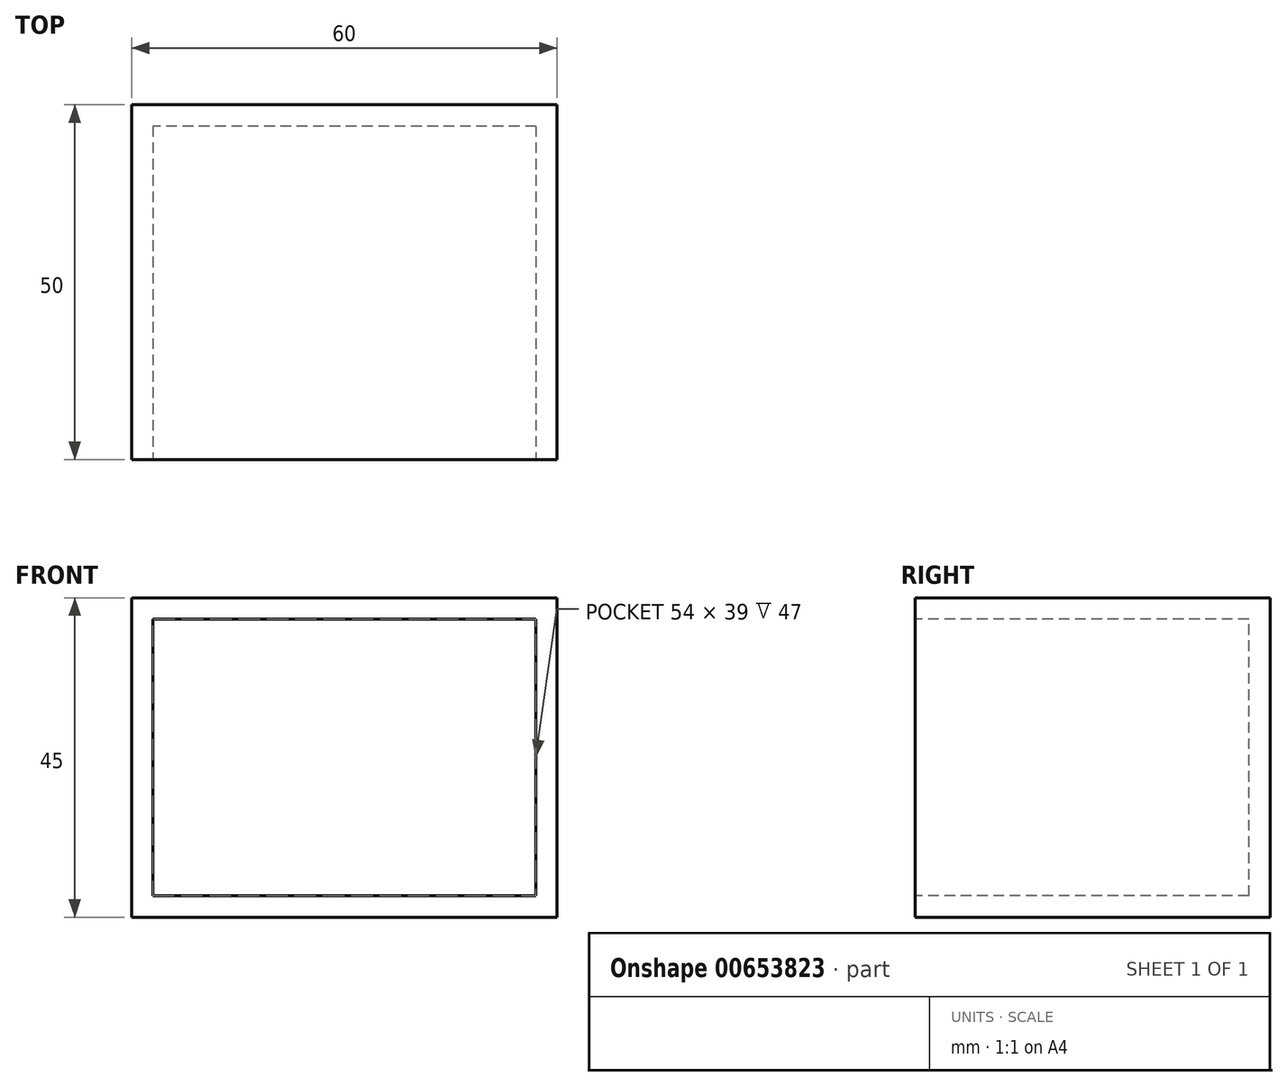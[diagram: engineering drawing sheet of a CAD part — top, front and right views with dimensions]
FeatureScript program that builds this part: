
annotation { "Feature Type Name" : "Feature", "Feature Type Description" : "" }
export const myFeature = defineFeature(function(context is Context, id is Id, definition is map)
    precondition{}
    {
        {
            var Q0;
            Q0=qCreatedBy(makeId("Front.planeOp"),FACE);
            var sketch = newSketch(context, id + "F0", { "sketchPlane" : qUnion([Q0])});
            skLineSegment(sketch, "E0.bottom", {"start": v(-30, 22.5) * mm, "end": v(30, 22.5) * mm});
            skLineSegment(sketch, "E0.top", {"start": v(-30, -22.5) * mm, "end": v(30, -22.5) * mm});
            skLineSegment(sketch, "E0.left", {"start": v(-30, 22.5) * mm, "end": v(-30, -22.5) * mm});
            skLineSegment(sketch, "E0.right", {"start": v(30, 22.5) * mm, "end": v(30, -22.5) * mm});
            skPoint(sketch, "E0.middle", {"position": v(0, 0) * mm});
            skSolve(sketch);
        }
        {
            var Q0;
            Q0=makeQuery(id+"F0.imprint","IMPRINT",FACE,{"disambiguationData":[TD([[makeQuery(id+"F0.imprint","IMPRINT",EDGE,{"derivedFrom":sQuery(id+"F0.wireOp",EDGE,"E0.bottom")}),-1.0]])]});
            extrude(context, id + "F1", {"entities" : qUnion([Q0]), "depth" : 50 * mm, "offsetDistance" : 25 * mm});
        }
        {
            var Q0;
            Q0=makeQuery(id+"F1.opExtrude","CAP_FACE",FACE,{"disambiguationData":[OSD([sQuery(id+"F0.wireOp",EDGE,"E0.bottom"),sQuery(id+"F0.wireOp",EDGE,"E0.top"),sQuery(id+"F0.wireOp",EDGE,"E0.left"),sQuery(id+"F0.wireOp",EDGE,"E0.right")])],"isStart":false});
            var sketch = newSketch(context, id + "F2", { "sketchPlane" : qUnion([Q0])});
            skLineSegment(sketch, "E1.0", {"start": v(-27, 19.5) * mm, "end": v(27, 19.5) * mm});
            skLineSegment(sketch, "E1.1", {"start": v(-27, 19.5) * mm, "end": v(-27, -19.5) * mm});
            skLineSegment(sketch, "E1.2", {"start": v(-27, -19.5) * mm, "end": v(27, -19.5) * mm});
            skLineSegment(sketch, "E1.3", {"start": v(27, 19.5) * mm, "end": v(27, -19.5) * mm});
            skSolve(sketch);
        }
        {
            var Q0;
            Q0=makeQuery(id+"F2.imprint","IMPRINT",FACE,{"disambiguationData":[TD([[makeQuery(id+"F2.imprint","IMPRINT",EDGE,{"derivedFrom":sQuery(id+"F2.wireOp",EDGE,"E1.0")}),-1.0]])]});
            var Q1;
            Q1=makeQuery(id+"F1.opExtrude","CAP_FACE",FACE,{"disambiguationData":[OSD([sQuery(id+"F0.wireOp",EDGE,"E0.bottom"),sQuery(id+"F0.wireOp",EDGE,"E0.top"),sQuery(id+"F0.wireOp",EDGE,"E0.left"),sQuery(id+"F0.wireOp",EDGE,"E0.right")])],"isStart":true});
            extrude(context, id + "F3", {"entities" : qUnion([Q0]), "operationType" : NewBodyOperationType.REMOVE, "endBound" : BoundingType.UP_TO_SURFACE, "oppositeDirection" : true, "depth" : 25 * mm, "endBoundEntityFace" : qUnion([Q1]), "hasOffset" : true, "offsetDistance" : 3 * mm});
        }
    });
